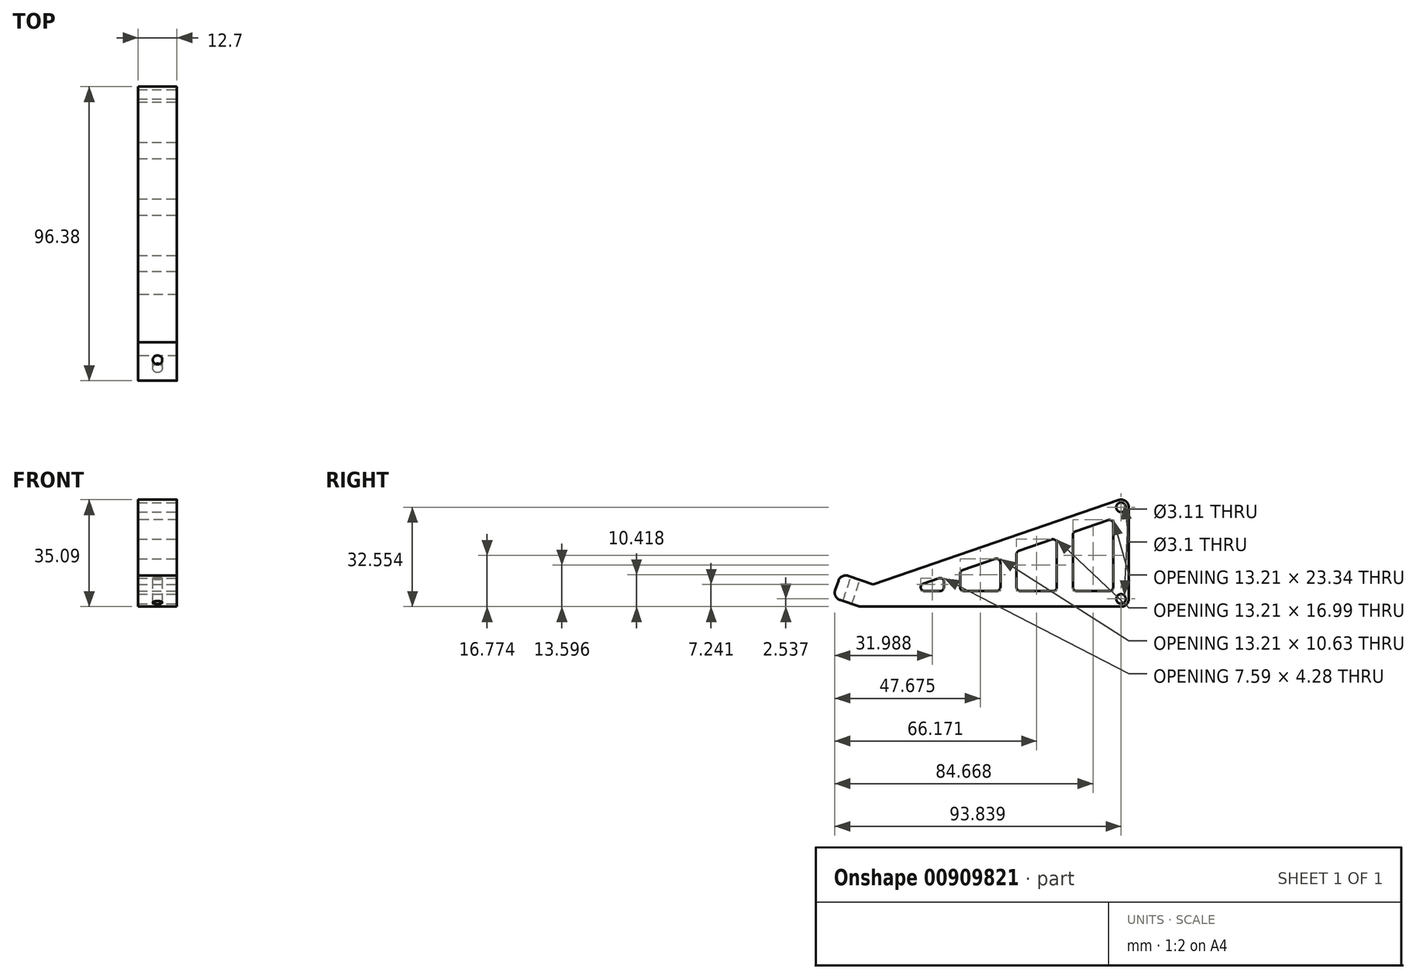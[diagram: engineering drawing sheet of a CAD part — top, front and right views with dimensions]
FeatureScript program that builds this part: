
annotation { "Feature Type Name" : "Feature", "Feature Type Description" : "" }
export const myFeature = defineFeature(function(context is Context, id is Id, definition is map)
    precondition{}
    {
        {
            var Q0;
            Q0=qCreatedBy(makeId("Right.planeOp"),FACE);
            var sketch = newSketch(context, id + "F0", { "sketchPlane" : qUnion([Q0])});
            skLineSegment(sketch, "E0", {"start": v(66.03, 57.35) * mm, "end": v(-39.08, 21.24) * mm});
            skLineSegment(sketch, "E1", {"start": v(-39.08, 21.24) * mm, "end": v(66.03, 21.24) * mm});
            skLineSegment(sketch, "E2", {"start": v(66.03, 21.24) * mm, "end": v(66.03, 57.35) * mm});
            skLineSegment(sketch, "E3", {"start": v(-22.23, 27.03) * mm, "end": v(-22.23, 21.24) * mm});
            skSolve(sketch);
        }
        {
            var Q0;
            {var subQ0=sQuery(id+"F0.wireOp",EDGE,"E2");Q0=makeQuery(id+"F0.imprint","IMPRINT",FACE,{"disambiguationData":[TD([[makeQuery(id+"F0.imprint","IMPRINT",EDGE,{"derivedFrom":subQ0}),1.0]])]});}
            extrude(context, id + "F1", {"entities" : qUnion([Q0]), "depth" : 12.7 * mm, "offsetDistance" : 25.4 * mm});
        }
        {
            var Q0;
            Q0=makeQuery(id+"F1.opExtrude","CAP_FACE",FACE,{"disambiguationData":[OSD([sQuery(id+"F0.wireOp",EDGE,"E0"),sQuery(id+"F0.wireOp",EDGE,"E1"),sQuery(id+"F0.wireOp",EDGE,"E2"),sQuery(id+"F0.wireOp",EDGE,"E3")])],"isStart":false});
            var sketch = newSketch(context, id + "F2", { "sketchPlane" : qUnion([Q0])});
            skLineSegment(sketch, "E4", {"start": v(-17.77, 28.56) * mm, "end": v(-28.35, 32.14) * mm});
            skLineSegment(sketch, "E5", {"start": v(-28.35, 32.14) * mm, "end": v(-31.03, 24.22) * mm});
            skLineSegment(sketch, "E6", {"start": v(-31.03, 24.22) * mm, "end": v(-22.23, 21.24) * mm});
            skSolve(sketch);
        }
        {
            var Q0;
            {var subQ1=sQuery(id+"F2.wireOp",EDGE,"E4");Q0=makeQuery(id+"F2.imprint","IMPRINT",FACE,{"disambiguationData":[TD([[makeQuery(id+"F2.imprint","IMPRINT",EDGE,{"derivedFrom":subQ1}),1.0]])]});}
            extrude(context, id + "F3", {"entities" : qUnion([Q0]), "operationType" : NewBodyOperationType.ADD, "depth" : 0 * mm, "offsetDistance" : 25.4 * mm, "hasSecondDirection" : true, "secondDirectionOppositeDirection" : true, "secondDirectionDepth" : 12.7 * mm});
        }
        {
            var Q0;
            Q0=makeQuery(id+"F3.opExtrude","SWEPT_EDGE",EDGE,{"disambiguationData":[OSD([sQuery(id+"F2.wireOp",EDGE,"E4"),sQuery(id+"F2.wireOp",EDGE,"E5")])]});
            var Q1;
            Q1=makeQuery(id+"F3.opExtrude","SWEPT_EDGE",EDGE,{"disambiguationData":[OSD([sQuery(id+"F2.wireOp",EDGE,"E5"),sQuery(id+"F2.wireOp",EDGE,"E6")])]});
            fillet(context, id + "F4", {"entities" : qUnion([Q0, Q1]), "radius" : 2.54 * mm, "tangentPropagation" : true, "allowEdgeOverflow" : false});
        }
        {
            var Q0;
            Q0=makeQuery(id+"F1.opExtrude","SWEPT_EDGE",EDGE,{"disambiguationData":[OSD([sQuery(id+"F0.wireOp",EDGE,"E0"),sQuery(id+"F0.wireOp",EDGE,"E2")])]});
            var Q1;
            Q1=makeQuery(id+"F1.opExtrude","SWEPT_EDGE",EDGE,{"disambiguationData":[OSD([sQuery(id+"F0.wireOp",EDGE,"E1"),sQuery(id+"F0.wireOp",EDGE,"E2")])]});
            fillet(context, id + "F5", {"entities" : qUnion([Q0, Q1]), "radius" : 2.54 * mm, "tangentPropagation" : true, "allowEdgeOverflow" : false});
        }
        {
            var Q0;
            Q0=makeQuery(id+"F3.opExtrude","SWEPT_FACE",FACE,{"disambiguationData":[OSD([sQuery(id+"F2.wireOp",EDGE,"E4")])]});
            var sketch = newSketch(context, id + "F6", { "sketchPlane" : qUnion([Q0])});
            skCircle(sketch, "E7", {"center": v(6.35, -32.1) * mm, "radius": 1.56 * mm});
            skPoint(sketch, "E7.centerSnap0", {"position": v(6.35, -26) * mm});
            skSolve(sketch);
        }
        {
            var Q0;
            Q0=makeQuery(id+"F6.imprint","IMPRINT",FACE,{"disambiguationData":[TD([[makeQuery(id+"F6.imprint","IMPRINT",EDGE,{"derivedFrom":sQuery(id+"F6.wireOp",EDGE,"E7")}),1.0]])]});
            extrude(context, id + "F7", {"entities" : qUnion([Q0]), "operationType" : NewBodyOperationType.REMOVE, "oppositeDirection" : true, "depth" : 25.4 * mm, "offsetDistance" : 25.4 * mm});
        }
        {
            var Q0;
            {var subQ0=sQuery(id+"F0.wireOp",EDGE,"E3");var subQ1=sQuery(id+"F0.wireOp",EDGE,"E0");Q0=makeQuery(id+"F3.boolean.opBoolean","MERGE",FACE,{"derivedFrom":[makeQuery(id+"F1.opExtrude","CAP_FACE",FACE,{"disambiguationData":[OSD([subQ1,sQuery(id+"F0.wireOp",EDGE,"E1"),sQuery(id+"F0.wireOp",EDGE,"E2"),subQ0])],"isStart":false}),makeQuery(id+"F3.opExtrude","CAP_FACE",FACE,{"disambiguationData":[OSD([subQ1,subQ0,sQuery(id+"F2.wireOp",EDGE,"E4"),sQuery(id+"F2.wireOp",EDGE,"E5"),sQuery(id+"F2.wireOp",EDGE,"E6")])],"isStart":false})]});}
            var sketch = newSketch(context, id + "F8", { "sketchPlane" : qUnion([Q0])});
            skCircle(sketch, "E8", {"center": v(63.49, 53.8) * mm, "radius": 1.55 * mm});
            skCircle(sketch, "E9", {"center": v(63.49, 23.78) * mm, "radius": 1.56 * mm});
            skSolve(sketch);
        }
        {
            var Q0;
            Q0=makeQuery(id+"F8.imprint","IMPRINT",FACE,{"disambiguationData":[TD([[makeQuery(id+"F8.imprint","IMPRINT",EDGE,{"derivedFrom":sQuery(id+"F8.wireOp",EDGE,"E8")}),1.0]])]});
            var Q1;
            Q1=makeQuery(id+"F8.imprint","IMPRINT",FACE,{"disambiguationData":[TD([[makeQuery(id+"F8.imprint","IMPRINT",EDGE,{"derivedFrom":sQuery(id+"F8.wireOp",EDGE,"E9")}),1.0]])]});
            extrude(context, id + "F9", {"entities" : qUnion([Q0, Q1]), "operationType" : NewBodyOperationType.REMOVE, "oppositeDirection" : true, "depth" : 25.4 * mm, "offsetDistance" : 25.4 * mm});
        }
        {
            var Q0;
            {var subQ0=sQuery(id+"F0.wireOp",EDGE,"E3");var subQ1=sQuery(id+"F0.wireOp",EDGE,"E0");Q0=makeQuery(id+"F3.boolean.opBoolean","MERGE",FACE,{"derivedFrom":[makeQuery(id+"F1.opExtrude","CAP_FACE",FACE,{"disambiguationData":[OSD([subQ1,sQuery(id+"F0.wireOp",EDGE,"E1"),sQuery(id+"F0.wireOp",EDGE,"E2"),subQ0])],"isStart":false}),makeQuery(id+"F3.opExtrude","CAP_FACE",FACE,{"disambiguationData":[OSD([subQ1,subQ0,sQuery(id+"F2.wireOp",EDGE,"E4"),sQuery(id+"F2.wireOp",EDGE,"E5"),sQuery(id+"F2.wireOp",EDGE,"E6")])],"isStart":false})]});}
            var sketch = newSketch(context, id + "F10", { "sketchPlane" : qUnion([Q0])});
            skLineSegment(sketch, "E10", {"start": v(60.92, 50.2) * mm, "end": v(47.71, 45.66) * mm});
            skLineSegment(sketch, "E11", {"start": v(47.71, 45.66) * mm, "end": v(42.43, 43.84) * mm});
            skLineSegment(sketch, "E12", {"start": v(42.43, 43.84) * mm, "end": v(29.22, 39.3) * mm});
            skLineSegment(sketch, "E13", {"start": v(29.22, 39.3) * mm, "end": v(23.93, 37.49) * mm});
            skLineSegment(sketch, "E14", {"start": v(23.93, 37.49) * mm, "end": v(10.72, 32.95) * mm});
            skLineSegment(sketch, "E15", {"start": v(10.72, 32.95) * mm, "end": v(5.43, 31.13) * mm});
            skLineSegment(sketch, "E16", {"start": v(5.43, 31.13) * mm, "end": v(-8.5, 26.34) * mm});
            skLineSegment(sketch, "E17", {"start": v(-8.5, 26.34) * mm, "end": v(60.92, 26.34) * mm});
            skLineSegment(sketch, "E18", {"start": v(60.92, 26.34) * mm, "end": v(60.92, 50.2) * mm});
            skLineSegment(sketch, "E19", {"start": v(47.71, 45.66) * mm, "end": v(47.71, 26.34) * mm});
            skLineSegment(sketch, "E20", {"start": v(42.43, 43.84) * mm, "end": v(42.43, 26.34) * mm});
            skLineSegment(sketch, "E21", {"start": v(29.22, 39.3) * mm, "end": v(29.22, 26.34) * mm});
            skLineSegment(sketch, "E22", {"start": v(23.93, 37.49) * mm, "end": v(23.93, 26.34) * mm});
            skLineSegment(sketch, "E23", {"start": v(5.43, 31.13) * mm, "end": v(5.43, 26.34) * mm});
            skLineSegment(sketch, "E24", {"start": v(10.72, 32.95) * mm, "end": v(10.72, 26.34) * mm});
            skSolve(sketch);
        }
        {
            var Q0;
            {var subQ0=sQuery(id+"F10.wireOp",EDGE,"E16");Q0=makeQuery(id+"F10.imprint","IMPRINT",FACE,{"disambiguationData":[TD([[makeQuery(id+"F10.imprint","IMPRINT",EDGE,{"derivedFrom":subQ0}),1.0]])]});}
            var Q1;
            Q1=makeQuery(id+"F10.imprint","IMPRINT",FACE,{"disambiguationData":[TD([[makeQuery(id+"F10.imprint","IMPRINT",EDGE,{"derivedFrom":sQuery(id+"F10.wireOp",EDGE,"E14")}),1.0]])]});
            var Q2;
            Q2=makeQuery(id+"F10.imprint","IMPRINT",FACE,{"disambiguationData":[TD([[makeQuery(id+"F10.imprint","IMPRINT",EDGE,{"derivedFrom":sQuery(id+"F10.wireOp",EDGE,"E12")}),1.0]])]});
            var Q3;
            Q3=makeQuery(id+"F10.imprint","IMPRINT",FACE,{"disambiguationData":[TD([[makeQuery(id+"F10.imprint","IMPRINT",EDGE,{"derivedFrom":sQuery(id+"F10.wireOp",EDGE,"E10")}),1.0]])]});
            extrude(context, id + "F11", {"entities" : qUnion([Q0, Q1, Q2, Q3]), "operationType" : NewBodyOperationType.REMOVE, "oppositeDirection" : true, "depth" : 25.4 * mm, "offsetDistance" : 25.4 * mm});
        }
        {
            var Q0;
            Q0=makeQuery(id+"F11.boolean.opBoolean","COPY",EDGE,{"derivedFrom":makeQuery(id+"F11.opExtrude","SWEPT_EDGE",EDGE,{"disambiguationData":[OSD([sQuery(id+"F10.wireOp",EDGE,"E10"),sQuery(id+"F10.wireOp",EDGE,"E18")])]})});
            var Q1;
            Q1=makeQuery(id+"F11.boolean.opBoolean","COPY",EDGE,{"derivedFrom":makeQuery(id+"F11.opExtrude","SWEPT_EDGE",EDGE,{"disambiguationData":[OSD([sQuery(id+"F10.wireOp",EDGE,"E17"),sQuery(id+"F10.wireOp",EDGE,"E19")])]})});
            var Q2;
            Q2=makeQuery(id+"F11.boolean.opBoolean","COPY",EDGE,{"derivedFrom":makeQuery(id+"F11.opExtrude","SWEPT_EDGE",EDGE,{"disambiguationData":[OSD([sQuery(id+"F10.wireOp",EDGE,"E10"),sQuery(id+"F10.wireOp",EDGE,"E11"),sQuery(id+"F10.wireOp",EDGE,"E19")])]})});
            var Q3;
            Q3=makeQuery(id+"F11.boolean.opBoolean","COPY",EDGE,{"derivedFrom":makeQuery(id+"F11.opExtrude","SWEPT_EDGE",EDGE,{"disambiguationData":[OSD([sQuery(id+"F10.wireOp",EDGE,"E12"),sQuery(id+"F10.wireOp",EDGE,"E13"),sQuery(id+"F10.wireOp",EDGE,"E21")])]})});
            var Q4;
            Q4=makeQuery(id+"F11.boolean.opBoolean","COPY",EDGE,{"derivedFrom":makeQuery(id+"F11.opExtrude","SWEPT_EDGE",EDGE,{"disambiguationData":[OSD([sQuery(id+"F10.wireOp",EDGE,"E14"),sQuery(id+"F10.wireOp",EDGE,"E15"),sQuery(id+"F10.wireOp",EDGE,"E24")])]})});
            var Q5;
            Q5=makeQuery(id+"F11.boolean.opBoolean","COPY",EDGE,{"derivedFrom":makeQuery(id+"F11.opExtrude","SWEPT_EDGE",EDGE,{"disambiguationData":[OSD([sQuery(id+"F10.wireOp",EDGE,"E17"),sQuery(id+"F10.wireOp",EDGE,"E18")])]})});
            var Q6;
            Q6=makeQuery(id+"F11.boolean.opBoolean","COPY",EDGE,{"derivedFrom":makeQuery(id+"F11.opExtrude","SWEPT_EDGE",EDGE,{"disambiguationData":[OSD([sQuery(id+"F10.wireOp",EDGE,"E17"),sQuery(id+"F10.wireOp",EDGE,"E20")])]})});
            var Q7;
            Q7=makeQuery(id+"F11.boolean.opBoolean","COPY",EDGE,{"derivedFrom":makeQuery(id+"F11.opExtrude","SWEPT_EDGE",EDGE,{"disambiguationData":[OSD([sQuery(id+"F10.wireOp",EDGE,"E17"),sQuery(id+"F10.wireOp",EDGE,"E23")])]})});
            var Q8;
            Q8=makeQuery(id+"F11.boolean.opBoolean","COPY",EDGE,{"derivedFrom":makeQuery(id+"F11.opExtrude","SWEPT_EDGE",EDGE,{"disambiguationData":[OSD([sQuery(id+"F10.wireOp",EDGE,"E17"),sQuery(id+"F10.wireOp",EDGE,"E22")])]})});
            var Q9;
            Q9=makeQuery(id+"F11.boolean.opBoolean","COPY",EDGE,{"derivedFrom":makeQuery(id+"F11.opExtrude","SWEPT_EDGE",EDGE,{"disambiguationData":[OSD([sQuery(id+"F10.wireOp",EDGE,"E11"),sQuery(id+"F10.wireOp",EDGE,"E12"),sQuery(id+"F10.wireOp",EDGE,"E20")])]})});
            var Q10;
            Q10=makeQuery(id+"F11.boolean.opBoolean","COPY",EDGE,{"derivedFrom":makeQuery(id+"F11.opExtrude","SWEPT_EDGE",EDGE,{"disambiguationData":[OSD([sQuery(id+"F10.wireOp",EDGE,"E13"),sQuery(id+"F10.wireOp",EDGE,"E14"),sQuery(id+"F10.wireOp",EDGE,"E22")])]})});
            var Q11;
            Q11=makeQuery(id+"F11.boolean.opBoolean","COPY",EDGE,{"derivedFrom":makeQuery(id+"F11.opExtrude","SWEPT_EDGE",EDGE,{"disambiguationData":[OSD([sQuery(id+"F10.wireOp",EDGE,"E15"),sQuery(id+"F10.wireOp",EDGE,"E16"),sQuery(id+"F10.wireOp",EDGE,"E23")])]})});
            var Q12;
            Q12=makeQuery(id+"F11.boolean.opBoolean","COPY",EDGE,{"derivedFrom":makeQuery(id+"F11.opExtrude","SWEPT_EDGE",EDGE,{"disambiguationData":[OSD([sQuery(id+"F10.wireOp",EDGE,"E16"),sQuery(id+"F10.wireOp",EDGE,"E17")])]})});
            var Q13;
            Q13=makeQuery(id+"F11.boolean.opBoolean","COPY",EDGE,{"derivedFrom":makeQuery(id+"F11.opExtrude","SWEPT_EDGE",EDGE,{"disambiguationData":[OSD([sQuery(id+"F10.wireOp",EDGE,"E17"),sQuery(id+"F10.wireOp",EDGE,"E24")])]})});
            var Q14;
            Q14=makeQuery(id+"F11.boolean.opBoolean","COPY",EDGE,{"derivedFrom":makeQuery(id+"F11.opExtrude","SWEPT_EDGE",EDGE,{"disambiguationData":[OSD([sQuery(id+"F10.wireOp",EDGE,"E17"),sQuery(id+"F10.wireOp",EDGE,"E21")])]})});
            fillet(context, id + "F12", {"entities" : qUnion([Q0, Q1, Q2, Q3, Q4, Q5, Q6, Q7, Q8, Q9, Q10, Q11, Q12, Q13, Q14]), "radius" : 1.27 * mm, "tangentPropagation" : true, "allowEdgeOverflow" : false});
        }
    });
